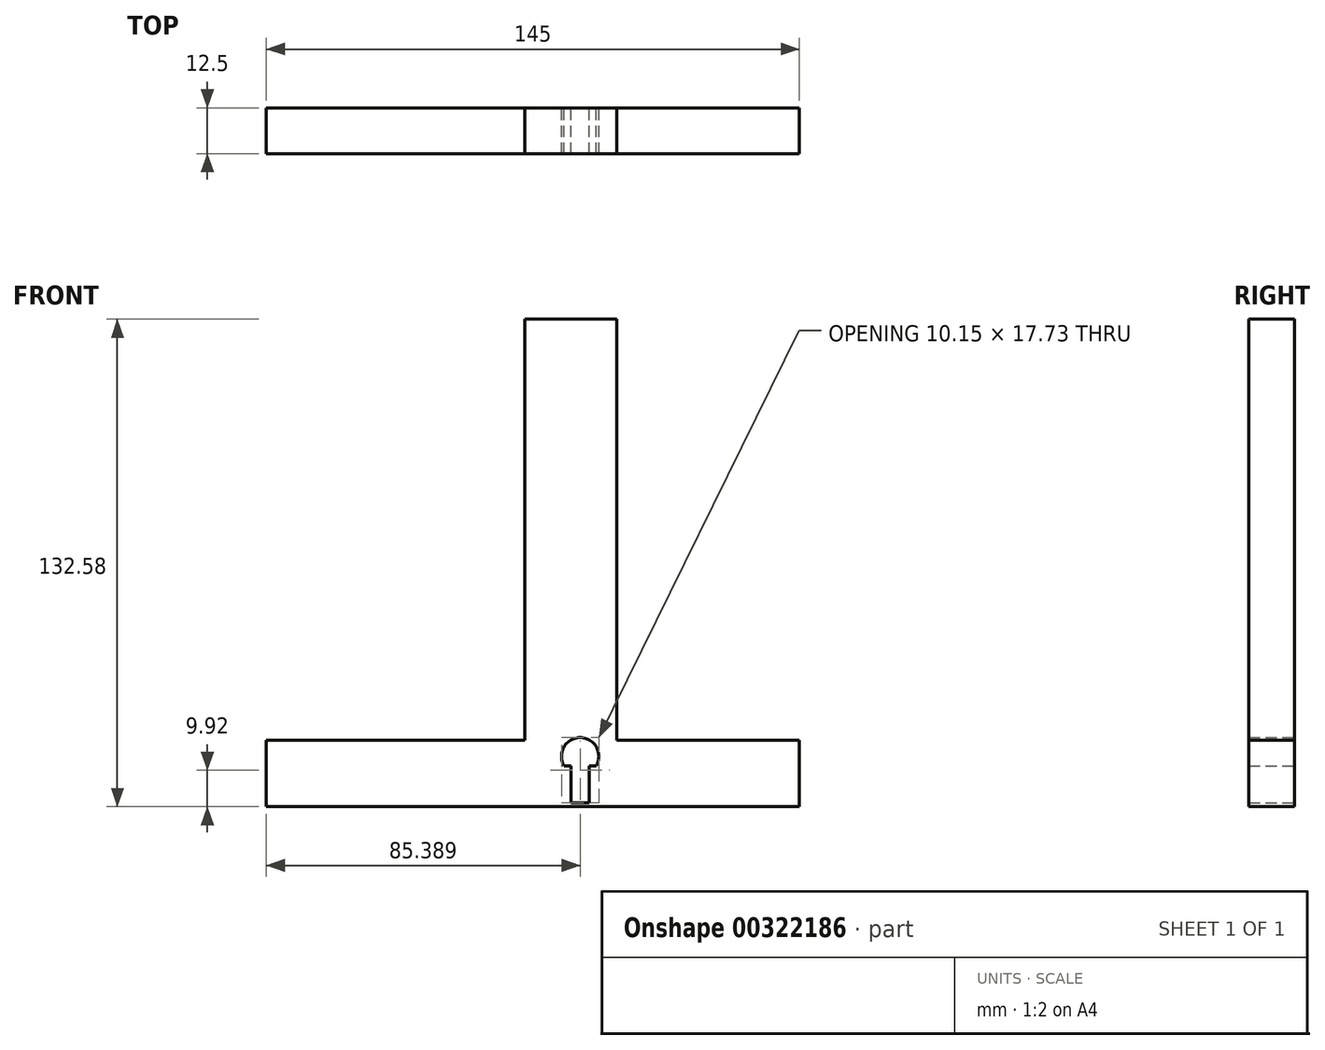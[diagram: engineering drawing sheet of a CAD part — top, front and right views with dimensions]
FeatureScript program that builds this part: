
annotation { "Feature Type Name" : "Feature", "Feature Type Description" : "" }
export const myFeature = defineFeature(function(context is Context, id is Id, definition is map)
    precondition{}
    {
        {
            var Q0;
            Q0=qCreatedBy(makeId("Front.planeOp"),FACE);
            var sketch = newSketch(context, id + "F0", { "sketchPlane" : qUnion([Q0])});
            skLineSegment(sketch, "E0.bottom", {"start": v(72.5, 9.06) * mm, "end": v(22.89, 9.06) * mm});
            skLineSegment(sketch, "E0.top", {"start": v(72.5, -9.06) * mm, "end": v(-72.5, -9.06) * mm});
            skLineSegment(sketch, "E0.left", {"start": v(72.5, 9.06) * mm, "end": v(72.5, -9.06) * mm});
            skLineSegment(sketch, "E0.right", {"start": v(-72.5, 9.06) * mm, "end": v(-72.5, -9.06) * mm});
            skLineSegment(sketch, "E1.top", {"start": v(22.89, 123.52) * mm, "end": v(-2.11, 123.52) * mm});
            skLineSegment(sketch, "E1.left", {"start": v(22.89, 9.06) * mm, "end": v(22.89, 123.52) * mm});
            skLineSegment(sketch, "E1.right", {"start": v(-2.11, 9.06) * mm, "end": v(-2.11, 123.52) * mm});
            skPoint(sketch, "E1.middle", {"position": v(-21.85, 53.91) * mm});
            skLineSegment(sketch, "E2.trimOffspring", {"start": v(-2.11, 9.06) * mm, "end": v(-72.5, 9.06) * mm});
            skLineSegment(sketch, "E3", {"start": v(8.56, 2) * mm, "end": v(10.39, 2) * mm});
            skArc(sketch, "E4", {"start": v(17.22, 2) * mm, "mid": v(12.89, 9.72) * mm, "end": v(8.56, 2) * mm});
            skPoint(sketch, "E4.centerSnap0", {"position": v(12.89, 2) * mm});
            skLineSegment(sketch, "E5.bottom", {"start": v(15.39, -8) * mm, "end": v(10.39, -8) * mm});
            skLineSegment(sketch, "E5.left", {"start": v(15.39, -8) * mm, "end": v(15.39, 2) * mm});
            skLineSegment(sketch, "E5.right", {"start": v(10.39, -8) * mm, "end": v(10.39, 2) * mm});
            skPoint(sketch, "E5.middle", {"position": v(10.14, 1.66) * mm});
            skLineSegment(sketch, "E6.trimOffspring", {"start": v(15.39, 2) * mm, "end": v(17.22, 2) * mm});
            skSolve(sketch);
        }
        {
            var Q0;
            Q0=makeQuery(id+"F0.imprint","IMPRINT",FACE,{"disambiguationData":[TD([[makeQuery(id+"F0.imprint","IMPRINT",EDGE,{"derivedFrom":sQuery(id+"F0.wireOp",EDGE,"E0.bottom")}),1.0]])]});
            extrude(context, id + "F1", {"entities" : qUnion([Q0]), "endBound" : BoundingType.SYMMETRIC, "depth" : 12.5 * mm});
        }
    });
